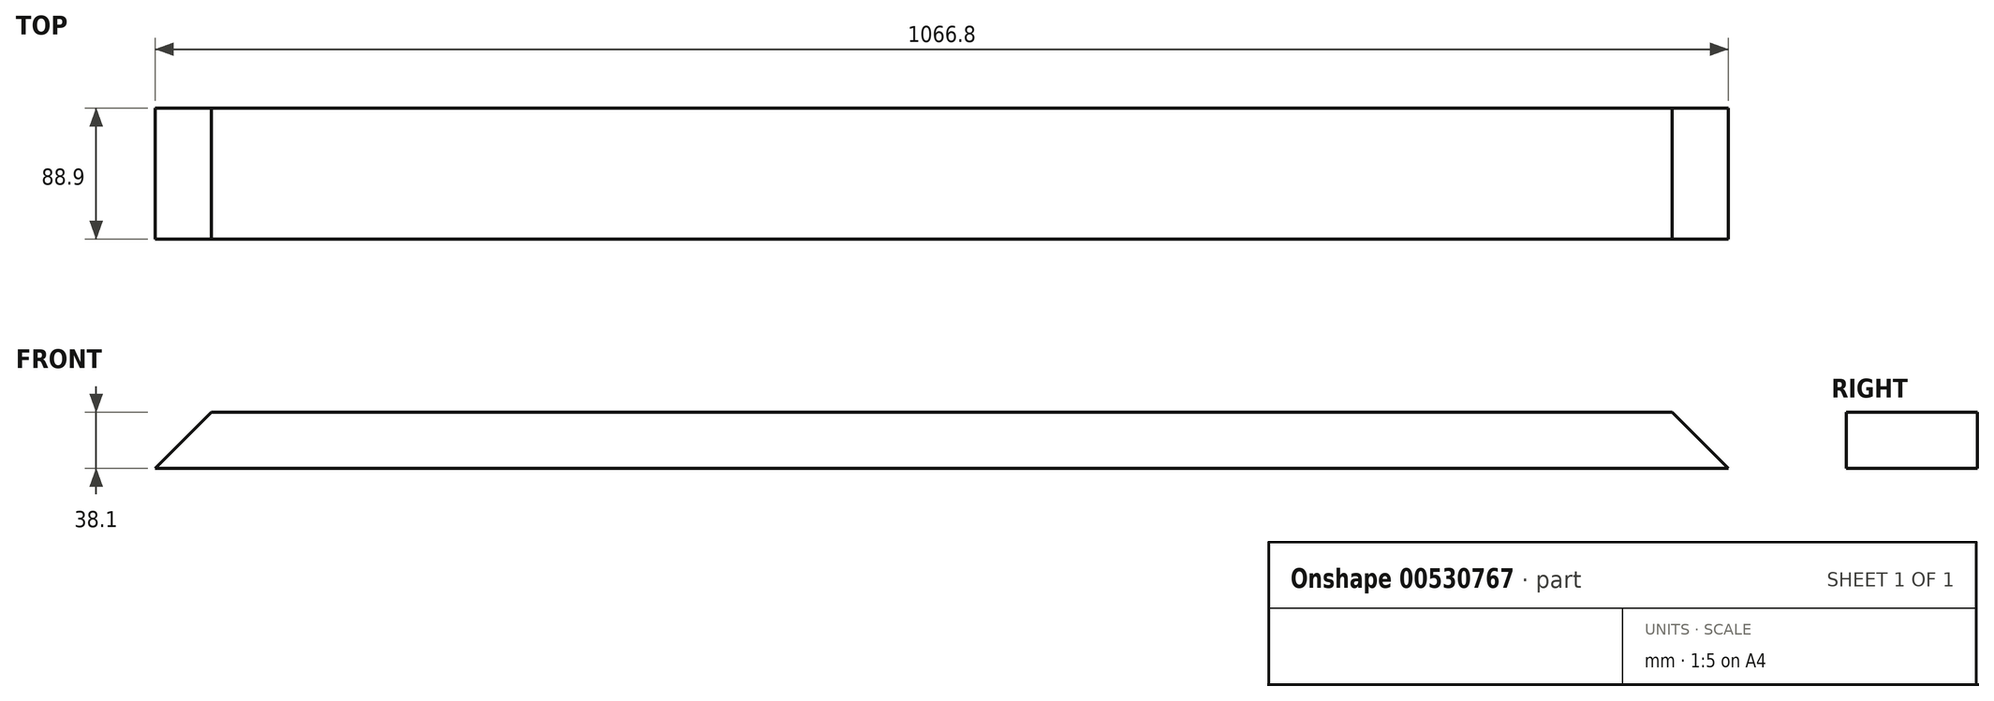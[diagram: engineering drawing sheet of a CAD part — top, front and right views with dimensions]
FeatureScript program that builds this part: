
annotation { "Feature Type Name" : "Feature", "Feature Type Description" : "" }
export const myFeature = defineFeature(function(context is Context, id is Id, definition is map)
    precondition{}
    {
        {
            var Q0;
            Q0=qCreatedBy(makeId("Front.planeOp"),FACE);
            var sketch = newSketch(context, id + "F0", { "sketchPlane" : qUnion([Q0])});
            skLineSegment(sketch, "E0", {"start": v(0, 0) * mm, "end": v(-1066.8, 0) * mm});
            skLineSegment(sketch, "E1", {"start": v(-1066.8, 0) * mm, "end": v(-1028.7, 38.1) * mm});
            skLineSegment(sketch, "E2", {"start": v(-1028.7, 38.1) * mm, "end": v(-38.1, 38.1) * mm});
            skLineSegment(sketch, "E3", {"start": v(-38.1, 38.1) * mm, "end": v(0, 0) * mm});
            skSolve(sketch);
        }
        {
            var Q0;
            Q0=makeQuery(id+"F0.imprint","IMPRINT",FACE,{"disambiguationData":[TD([[makeQuery(id+"F0.imprint","IMPRINT",EDGE,{"derivedFrom":sQuery(id+"F0.wireOp",EDGE,"E0")}),-1.0]])]});
            extrude(context, id + "F1", {"entities" : qUnion([Q0]), "depth" : 88.9 * mm, "offsetDistance" : 25.4 * mm});
        }
    });
